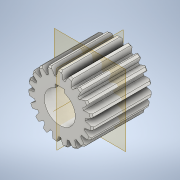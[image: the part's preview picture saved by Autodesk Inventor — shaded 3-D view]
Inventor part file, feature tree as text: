
AUTODESK INVENTOR PART (.ipt)
format: ipt  version: 2020 (Build 240168000, 168)  size: 365,056 bytes
history: native  units: mm (DEFAULTED — no unit token found)
features: plane x5, sketch x4, other x3, extrude x2, revolve x1, mirror x1
ambient origin geometry x8: Origin, YZ Plane, XZ Plane, XY Plane, X Axis, Y Axis, Z Axis, Center Point
bodies: Solid1 (feature_tree)
feature tree (16):
  extrude  "Extrusion1"  Depth=78.0mm TaperAngle=0.0deg
  plane  "Work Plane2"
  plane  "Work Plane8"
  plane  "Work Plane9"
  other  "正齿轮"
  extrude  "拉伸2"  Depth=10.0mm TaperAngle=0.0deg
  plane  "工作平面11"
  plane  "工作平面12"
  sketch  "草图4"  dims[d39=0.0mm d41=0.0mm d43=276.0mm d46=276.0mm d47=0.0mm d48=0.0mm d49=40.0mm d50=12.0mm d51=8.0mm d52=3.5mm d53=10.0mm d54=0.0mm d55=2.0mm d56=2.0mm d57=90.0deg]
  other  "工作轴1"
  revolve  "旋转1"  [1 undecoded]
  mirror  "镜像1"
  sketch  "Sketch1"  dims[d0=84.0mm d1=78.0mm d2=0.0mm]
  sketch  "Sketch2"  dims[d3=76.0mm d4=10.0mm d5=0.0mm]
  other  "Srf1"
  sketch  "草图3"  dims[d16=276.0mm d17=0.0mm d34=1.65347mm]
note: 1 required parameter value undecoded (feature->parameter linkage not recoverable at this tier; creation-order binding heuristic only, values carry confidence <= 0.55)
